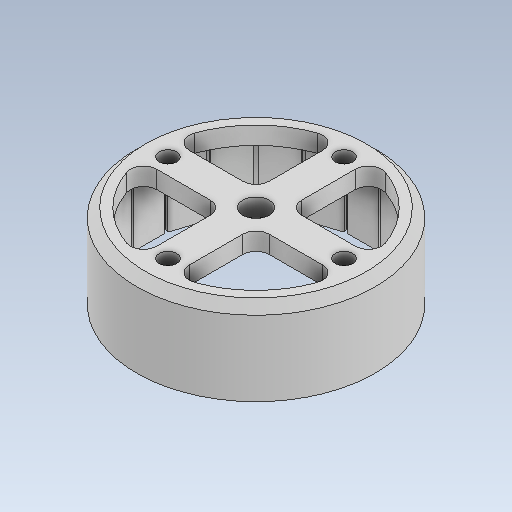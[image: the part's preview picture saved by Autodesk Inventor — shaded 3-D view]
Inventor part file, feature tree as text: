
AUTODESK INVENTOR PART (.ipt)
format: ipt  version: 2023 (Build 270158000, 158)  size: 305,152 bytes
history: native  units: mm
features: extrude x6, sketch x6, projected_geometry x3, chamfer x1, pattern_circular x1, fillet x1
ambient origin geometry x8: Origin, YZ Plane, XZ Plane, XY Plane, X Axis, Y Axis, Z Axis, Center Point
bodies: Solid1 (feature_tree)
feature tree (18):
  extrude  "Extrusion1"  Depth=9.5mm TaperAngle=0.0deg
  extrude  "Extrusion2"  Depth=3.7mm
  extrude  "Extrusion3"  Depth=3.7mm
  chamfer  "Chamfer1"  Distance=9.5mm
  extrude  "Extrusion4"  Depth=7.5mm TaperAngle=0.0deg
  extrude  "Extrusion5"  Depth=1.5mm
  pattern_circular  "Circular Pattern1"  [2 undecoded]
  extrude  "Extrusion6"  Depth=1.5mm
  fillet  "Fillet2"  Radius=0.7mm
  sketch  "Sketch1"  dims[d0=27.1mm d1=9.5mm d2=0.0mm]
  sketch  "Sketch2"  dims[d3=3.7mm d4=40.0mm]
  projected_geometry  "Projected Loop1"
  sketch  "Sketch3"  dims[d5=3.7mm d6=40.0mm]
  projected_geometry  "Projected Loop2"
  sketch  "Sketch4"  dims[d7=23.0mm d8=9.5mm d9=0.0mm]
  sketch  "Sketch5"  dims[d10=0.85mm d11=7.5mm d12=0.0mm]
  projected_geometry  "Projected Loop3"
  sketch  "Sketch6"  dims[d13=1.0mm d14=2.0mm d15=45.0deg d17=3.0mm d18=7.5mm d19=0.0mm d20=12.5mm d21=0.7mm d22=3.5mm d23=7.5mm d24=0.0mm d25=200.0mm d26=360.0deg d28=10.0mm d29=2.0mm d30=40.0mm d32=360.0deg d34=7.5mm d35=0.0mm d36=1.5mm]
note: 2 required parameter values undecoded (feature->parameter linkage not recoverable at this tier; creation-order binding heuristic only, values carry confidence <= 0.55)
